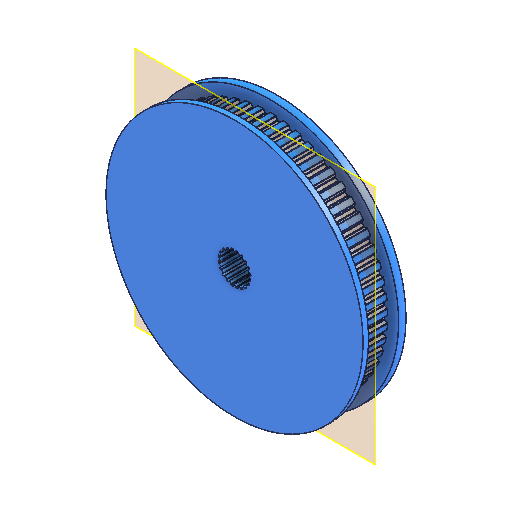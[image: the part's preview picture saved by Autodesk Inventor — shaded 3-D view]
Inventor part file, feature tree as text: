
AUTODESK INVENTOR PART (.ipt)
format: ipt  version: 2025.2 (Build 292293000, 293)  size: 1,184,256 bytes
history: native  units: in
note: dims shown in document units (in); Inventor stores cm internally (conversion verified against a paired STEP export)
features: sketch x6, extrude x5, plane x1
ambient origin geometry x8: Origin, YZ Plane, XZ Plane, XY Plane, X Axis, Y Axis, Z Axis, Center Point
bodies: Solid1 (feature_tree)
feature tree (12):
  extrude  "Extrusion1"  Depth=0.6181in TaperAngle=0.0deg
  plane  "Work Plane1"
  extrude  "Extrusion2"  Depth=3.388in
  extrude  "Extrusion3"  Depth=0.4331in
  extrude  "Extrusion5"  Depth=0.25in
  extrude  "Extrusion7"  Depth=0.25in
  sketch  "Sketch1"  dims[d0=3.7in d1=0.6181in d2=0.0in]
  sketch  "Sketch2"  dims[d3=-0.2953in d4=3.388in]
  sketch  "Sketch3"  dims[d8=0.0in d9=0.0in d13=0.25in]
  sketch  "Sketch5"  dims[d14=0.8in d15=0.25in]
  sketch  "Sketch8"  dims[d16=0.8in d21=0.0in d22=0.0in d23=0.6181in d24=0.0in d39=3.7in d52=22.8346in d54=360.0deg d56=0.4331in d57=0.0in]
  sketch  "Sketch Circular Pattern2"  dims[d5=0.4331in d6=0.0in d7=0.4724in]
